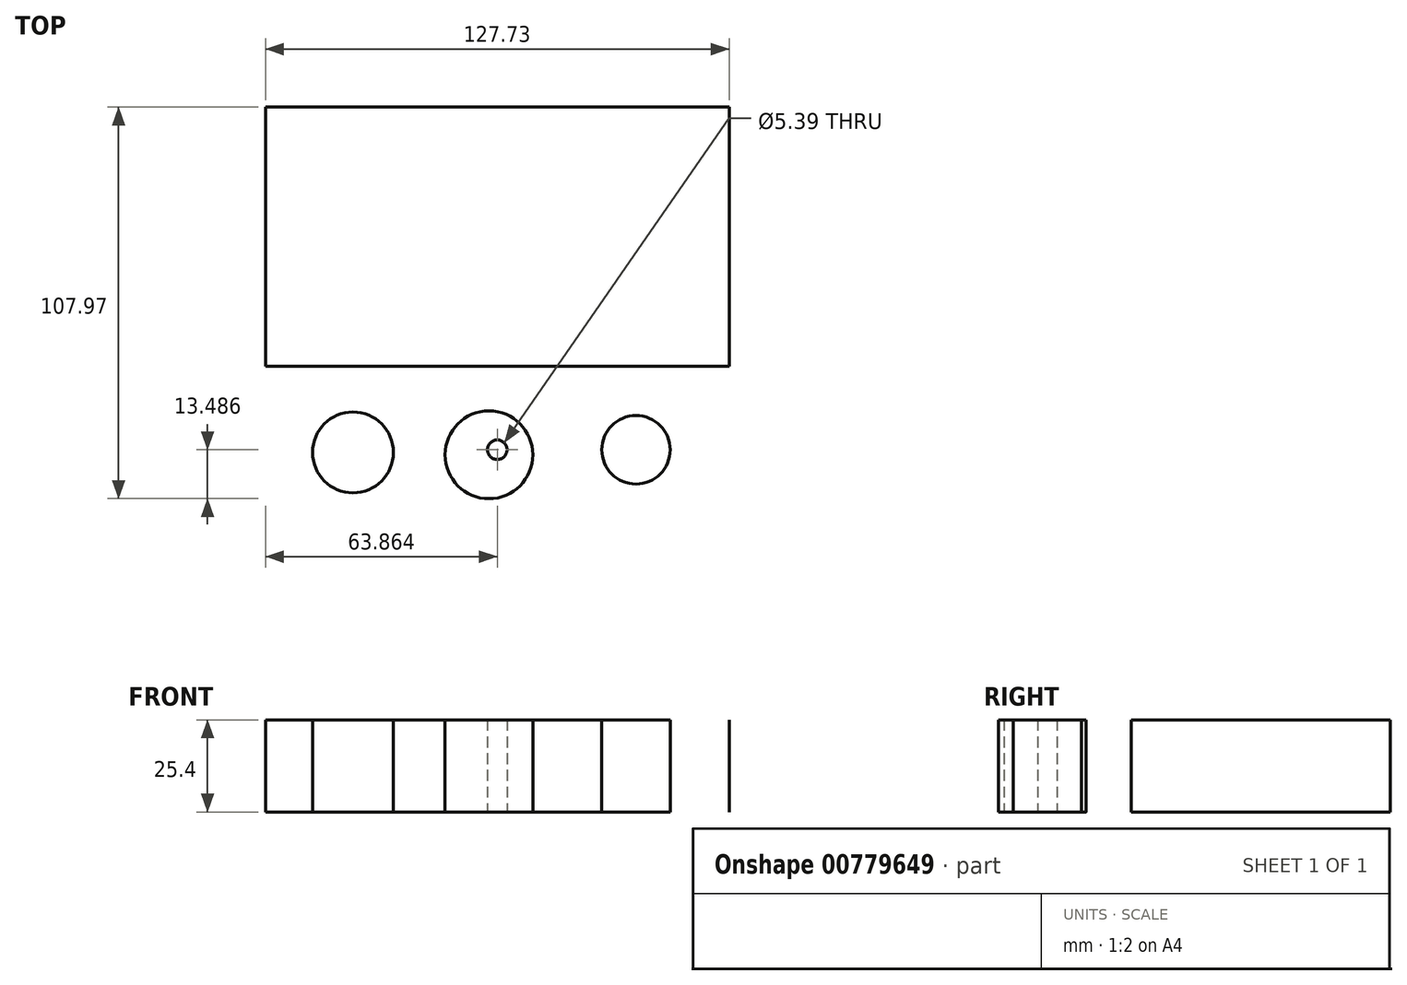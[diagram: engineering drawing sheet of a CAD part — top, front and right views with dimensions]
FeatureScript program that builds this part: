
annotation { "Feature Type Name" : "Feature", "Feature Type Description" : "" }
export const myFeature = defineFeature(function(context is Context, id is Id, definition is map)
    precondition{}
    {
        {
            var Q0;
            Q0=qCreatedBy(makeId("Top.planeOp"),FACE);
            var sketch = newSketch(context, id + "F0", { "sketchPlane" : qUnion([Q0])});
            skLineSegment(sketch, "E0.bottom", {"start": v(-70.57, 57.58) * mm, "end": v(57.16, 57.58) * mm});
            skLineSegment(sketch, "E0.top", {"start": v(-70.57, -13.85) * mm, "end": v(57.16, -13.85) * mm});
            skLineSegment(sketch, "E0.left", {"start": v(-70.57, 57.58) * mm, "end": v(-70.57, -13.85) * mm});
            skLineSegment(sketch, "E0.right", {"start": v(57.16, 57.58) * mm, "end": v(57.16, -13.85) * mm});
            skCircle(sketch, "E1", {"center": v(-46.48, -37.64) * mm, "radius": 11.15 * mm});
            skCircle(sketch, "E2", {"center": v(-6.7, -36.9) * mm, "radius": 2.7 * mm});
            skPoint(sketch, "E2.centerSnap0", {"position": v(-6.7, -13.85) * mm});
            skCircle(sketch, "E3", {"center": v(-9.01, -38.3) * mm, "radius": 12.1 * mm});
            skCircle(sketch, "E4", {"center": v(31.5, -36.9) * mm, "radius": 9.44 * mm});
            skSolve(sketch);
        }
        {
            var Q0;
            Q0=makeQuery(id+"F0.imprint","IMPRINT",FACE,{"disambiguationData":[TD([[makeQuery(id+"F0.imprint","IMPRINT",EDGE,{"derivedFrom":sQuery(id+"F0.wireOp",EDGE,"E0.bottom")}),-1.0]])]});
            var Q1;
            Q1=makeQuery(id+"F0.imprint","IMPRINT",FACE,{"disambiguationData":[TD([[makeQuery(id+"F0.imprint","IMPRINT",EDGE,{"derivedFrom":sQuery(id+"F0.wireOp",EDGE,"E4")}),1.0]])]});
            var Q2;
            Q2=makeQuery(id+"F0.imprint","IMPRINT",FACE,{"disambiguationData":[TD([[makeQuery(id+"F0.imprint","IMPRINT",EDGE,{"derivedFrom":sQuery(id+"F0.wireOp",EDGE,"E2")}),-1.0]])]});
            var Q3;
            Q3=makeQuery(id+"F0.imprint","IMPRINT",FACE,{"disambiguationData":[TD([[makeQuery(id+"F0.imprint","IMPRINT",EDGE,{"derivedFrom":sQuery(id+"F0.wireOp",EDGE,"E1")}),1.0]])]});
            extrude(context, id + "F1", {"entities" : qUnion([Q0, Q1, Q2, Q3]), "depth" : 25.4 * mm, "offsetDistance" : 25.4 * mm});
        }
    });
